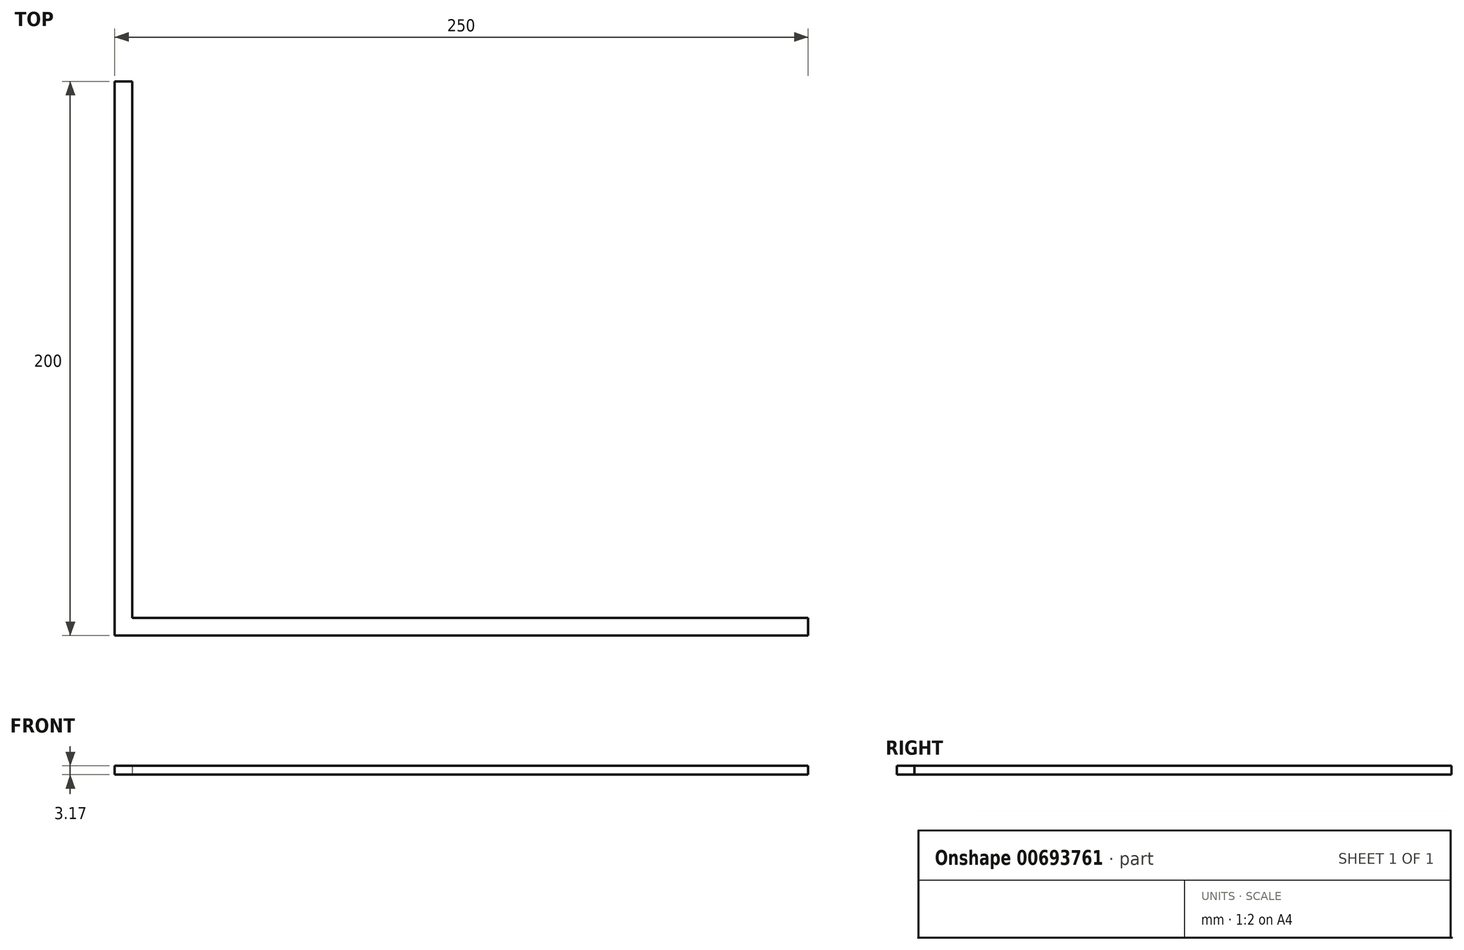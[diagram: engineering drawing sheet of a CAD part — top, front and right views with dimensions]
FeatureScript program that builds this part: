
annotation { "Feature Type Name" : "Feature", "Feature Type Description" : "" }
export const myFeature = defineFeature(function(context is Context, id is Id, definition is map)
    precondition{}
    {
        {
            var Q0;
            Q0=qCreatedBy(makeId("Top.planeOp"),FACE);
            var sketch = newSketch(context, id + "F0", { "sketchPlane" : qUnion([Q0])});
            skLineSegment(sketch, "E0", {"start": v(0, 0) * mm, "end": v(0, 200) * mm});
            skLineSegment(sketch, "E1", {"start": v(0, 0) * mm, "end": v(250, 0) * mm});
            skLineSegment(sketch, "E2.bottom", {"start": v(250, 0) * mm, "end": v(0, 0) * mm});
            skLineSegment(sketch, "E2.top", {"start": v(250, 6.35) * mm, "end": v(0, 6.35) * mm});
            skLineSegment(sketch, "E2.left", {"start": v(250, 0) * mm, "end": v(250, 6.35) * mm});
            skLineSegment(sketch, "E2.right", {"start": v(0, 0) * mm, "end": v(0, 6.35) * mm});
            skLineSegment(sketch, "E3.bottom", {"start": v(0, 200) * mm, "end": v(6.35, 200) * mm});
            skLineSegment(sketch, "E3.top", {"start": v(0, 0) * mm, "end": v(6.35, 0) * mm});
            skLineSegment(sketch, "E3.left", {"start": v(0, 200) * mm, "end": v(0, 0) * mm});
            skLineSegment(sketch, "E3.right", {"start": v(6.35, 200) * mm, "end": v(6.35, 0) * mm});
            skSolve(sketch);
        }
        {
            var Q0;
            Q0 = qSketchRegion(id + "F0", true);
            extrude(context, id + "F1", {"entities" : qUnion([Q0]), "depth" : 3.17 * mm, "offsetDistance" : 25.4 * mm});
        }
    });
